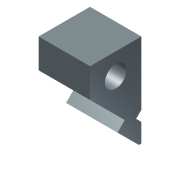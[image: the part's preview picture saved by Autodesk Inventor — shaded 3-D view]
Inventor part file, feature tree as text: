
AUTODESK INVENTOR PART (.ipt)
format: ipt  version: 2013 (Build 170138000, 138)  size: 188,928 bytes
history: native  units: in
note: dims shown in document units (in); Inventor stores cm internally (conversion verified against a paired STEP export)
features: other x2, sketch x2, extrude x1, imported_body x1
ambient origin geometry x8: Origin, YZ Plane, XZ Plane, XY Plane, X Axis, Y Axis, Z Axis, Center Point
feature tree (6):
  other  "product-name"
  other  "product-name1"
  extrude  "Extrusion1"  Depth=0.0004in TaperAngle=0.0deg
  sketch  "Sketch2"  dims[d3=0.2087in]
  imported_body  "Base1"
  sketch  "Sketch1"  dims[d0=0.1157in d1=0.0004in d2=0.0in]
